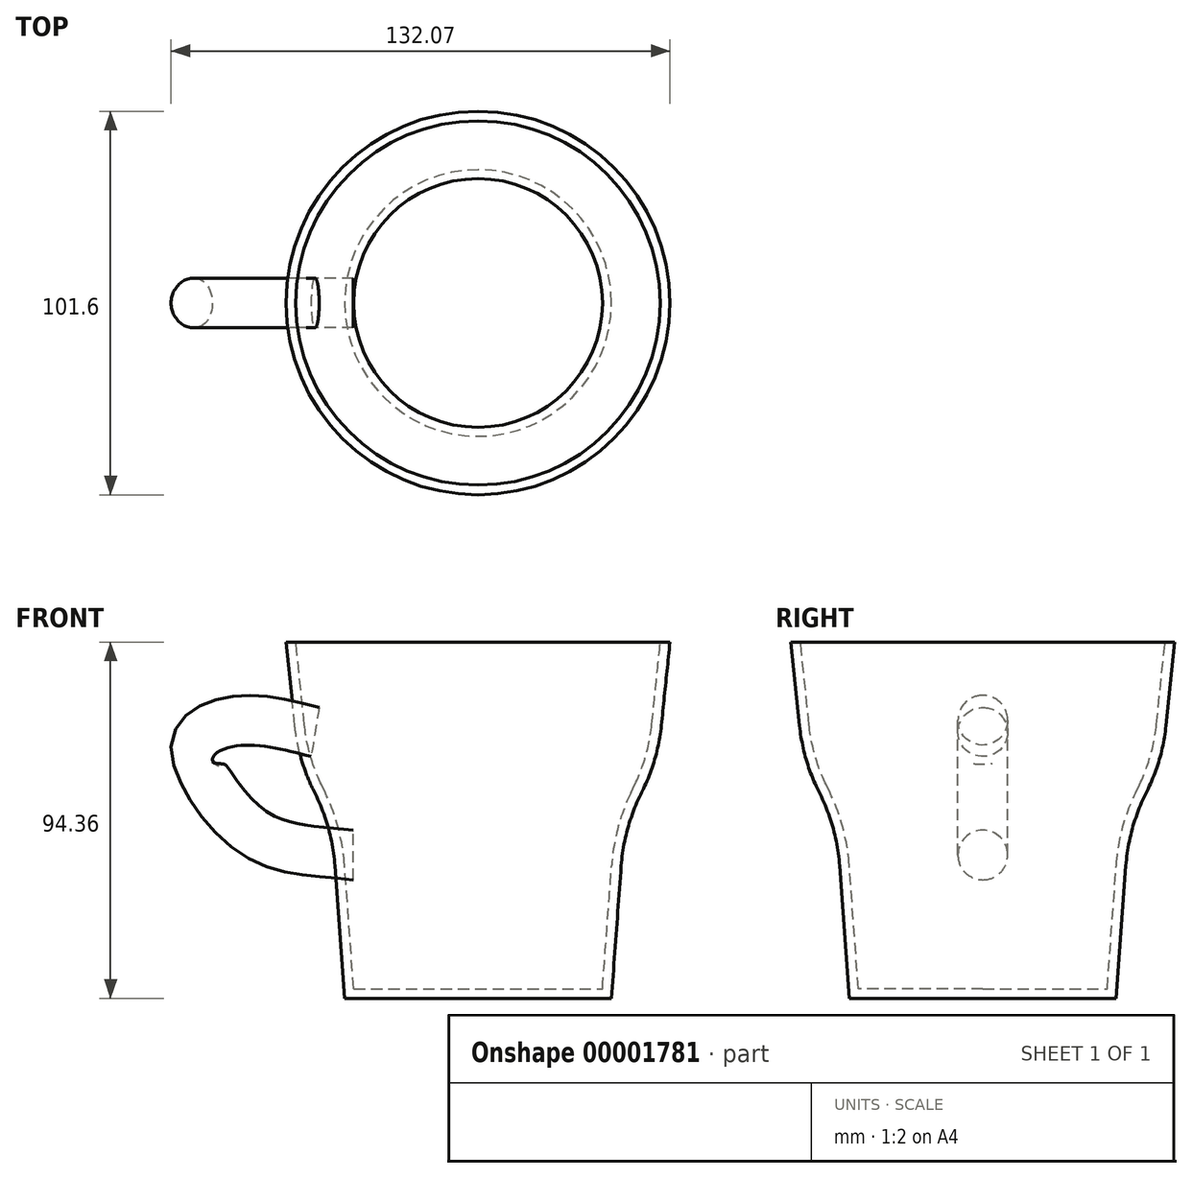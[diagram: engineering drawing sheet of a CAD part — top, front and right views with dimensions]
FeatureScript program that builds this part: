
annotation { "Feature Type Name" : "Feature", "Feature Type Description" : "" }
export const myFeature = defineFeature(function(context is Context, id is Id, definition is map)
    precondition{}
    {
        {
            var Q0;
            Q0=qCreatedBy(makeId("Front.planeOp"),FACE);
            var sketch = newSketch(context, id + "F0", { "sketchPlane" : qUnion([Q0])});
            skLineSegment(sketch, "E0", {"start": v(35.3, 0) * mm, "end": v(0, 0) * mm});
            skLineSegment(sketch, "E1", {"start": v(0, 0) * mm, "end": v(0, 94.36) * mm});
            skLineSegment(sketch, "E2", {"start": v(0, 94.36) * mm, "end": v(50.8, 94.36) * mm});
            skLineSegment(sketch, "E3", {"start": v(38.59, 44.69) * mm, "end": v(35.3, 0) * mm});
            skLineSegment(sketch, "E4", {"start": v(0, 94.36) * mm, "end": v(0, -25.62) * mm, "construction": true});
            skLineSegment(sketch, "E5", {"start": v(50.8, 94.36) * mm, "end": v(47.6, 63.44) * mm});
            skLineSegment(sketch, "E6", {"start": v(47.6, 63.44) * mm, "end": v(38.59, 44.69) * mm});
            skSolve(sketch);
        }
        {
            var Q0;
            Q0=makeQuery(id+"F0.imprint","IMPRINT",FACE,{"disambiguationData":[TD([[makeQuery(id+"F0.imprint","IMPRINT",EDGE,{"derivedFrom":sQuery(id+"F0.wireOp",EDGE,"E0")}),-1.0]])]});
            var Q1;
            Q1=sQuery(id+"F0.wireOp",EDGE,"E4");
            revolve(context, id + "F1", {"entities" : qUnion([Q0]), "axis" : qUnion([Q1]), "revolveType" : RevolveType.FULL});
        }
        {
            var Q0;
            Q0=makeQuery(id+"F1.opRevolve","SWEPT_EDGE",EDGE,{"disambiguationData":[OSD([sQuery(id+"F0.wireOp",EDGE,"E5"),sQuery(id+"F0.wireOp",EDGE,"E6")])]});
            fillet(context, id + "F2", {"entities" : qUnion([Q0]), "radius" : 50.8 * mm, "tangentPropagation" : true, "allowEdgeOverflow" : false});
        }
        {
            var Q0;
            Q0=makeQuery(id+"F1.opRevolve","SWEPT_EDGE",EDGE,{"disambiguationData":[OSD([sQuery(id+"F0.wireOp",EDGE,"E3"),sQuery(id+"F0.wireOp",EDGE,"E6")])]});
            fillet(context, id + "F3", {"entities" : qUnion([Q0]), "radius" : 50.8 * mm, "tangentPropagation" : true, "allowEdgeOverflow" : false});
        }
        {
            var Q0;
            Q0=qCreatedBy(makeId("Front.planeOp"),FACE);
            var sketch = newSketch(context, id + "F4", { "sketchPlane" : qUnion([Q0])});
            skPoint(sketch, "E7.0.end.orphan", {"position": v(37.88, 35.09) * mm});
            skPoint(sketch, "E7.0.start.orphan", {"position": v(-37.88, 35.09) * mm});
            skFitSpline(sketch, "E8", {"points": [v(-37.88, 35.09) * mm, v(-63.18, 42.88) * mm, v(-76.8, 67.75) * mm, v(-64.1, 76.53) * mm, v(-37.88, 72.57) * mm], "startDerivative": vector(-99.96, 10.38) * mm, "endDerivative": vector(103.45, -28.2) * mm});
            skSolve(sketch);
        }
        {
            var Q0;
            Q0=qCreatedBy(makeId("Right.planeOp"),FACE);
            cPlane(context, id + "F5", {"entities" : qUnion([Q0]), "cplaneType" : CPlaneType.OFFSET, "offset" : 33.02 * mm, "oppositeDirection" : true, "width" : 152.4 * mm, "height" : 152.4 * mm});
        }
        {
            var Q0;
            Q0=qCreatedBy(id+"F5.planeOp",FACE);
            var sketch = newSketch(context, id + "F6", { "sketchPlane" : qUnion([Q0])});
            skCircle(sketch, "E9", {"center": v(0, 37.96) * mm, "radius": 6.58 * mm});
            skSolve(sketch);
        }
        {
            var Q0;
            Q0=makeQuery(id+"F6.imprint","IMPRINT",FACE,{"disambiguationData":[TD([[makeQuery(id+"F6.imprint","IMPRINT",EDGE,{"derivedFrom":sQuery(id+"F6.wireOp",EDGE,"E9")}),1.0]])]});
            var Q1;
            Q1=sQuery(id+"F4.wireOp",EDGE,"E8");
            sweep(context, id + "F7", {"profiles" : qUnion([Q0]), "path" : qUnion([Q1])});
        }
        {
            var Q0;
            Q0=makeQuery(id+"F1.opRevolve","SWEPT_FACE",FACE,{"disambiguationData":[OSD([sQuery(id+"F0.wireOp",EDGE,"E2")])]});
            shell(context, id + "F8", {"entities" : qUnion([Q0]), "thickness" : 2.54 * mm});
        }
    });
